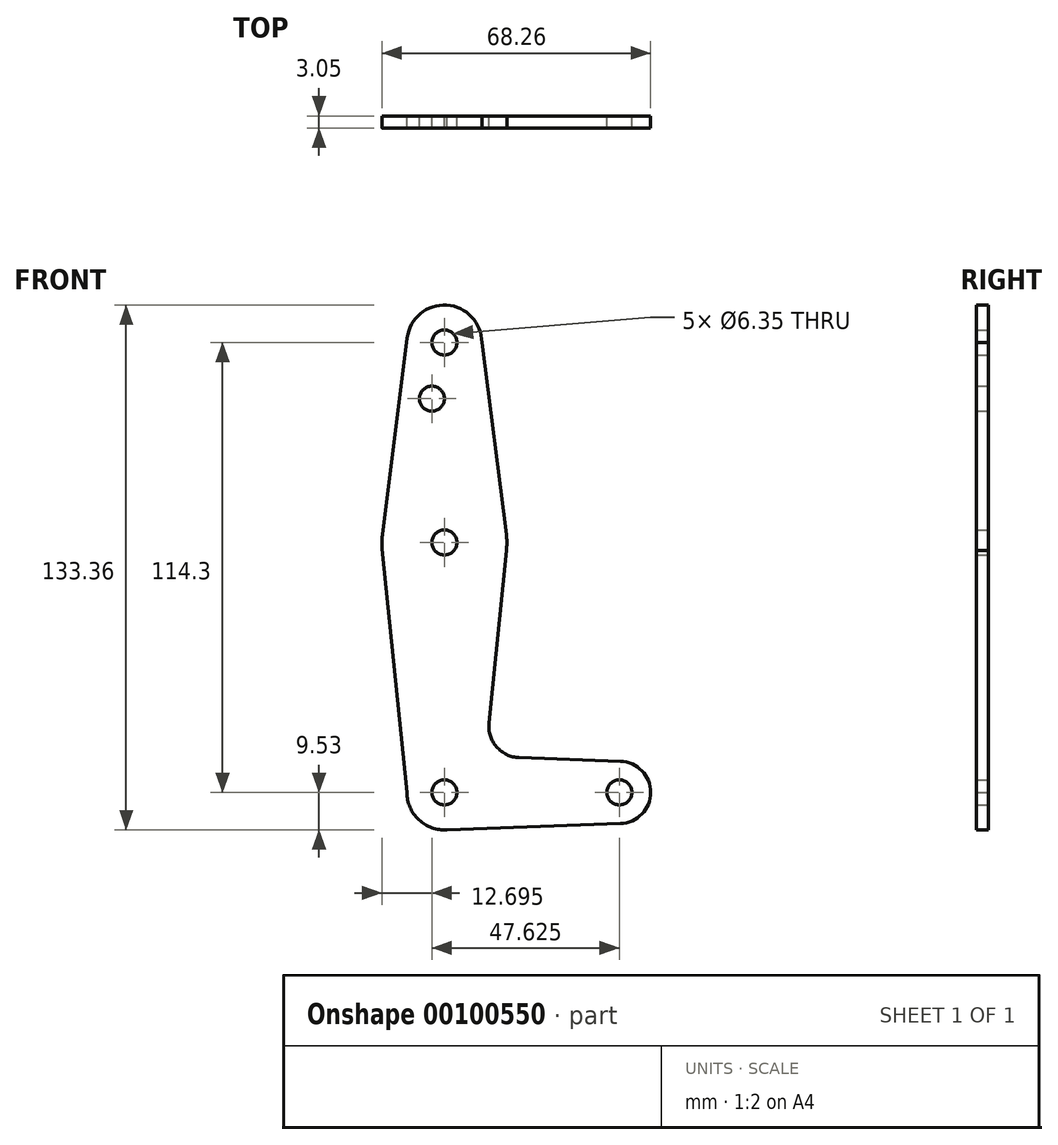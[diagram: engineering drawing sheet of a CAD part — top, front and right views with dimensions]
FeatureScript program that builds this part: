
annotation { "Feature Type Name" : "Feature", "Feature Type Description" : "" }
export const myFeature = defineFeature(function(context is Context, id is Id, definition is map)
    precondition{}
    {
        {
            var Q0;
            Q0=qCreatedBy(makeId("Front.planeOp"),FACE);
            var sketch = newSketch(context, id + "F0", { "sketchPlane" : qUnion([Q0])});
            skLineSegment(sketch, "E0", {"start": v(0, 114.3) * mm, "end": v(0, 0) * mm, "construction": true});
            skLineSegment(sketch, "E1", {"start": v(0, 0) * mm, "end": v(44.45, 0) * mm, "construction": true});
            skCircle(sketch, "E2", {"center": v(0, 114.3) * mm, "radius": 9.53 * mm});
            skCircle(sketch, "E3", {"center": v(0, 63.5) * mm, "radius": 15.88 * mm});
            skCircle(sketch, "E4", {"center": v(0, 0) * mm, "radius": 9.53 * mm});
            skCircle(sketch, "E5", {"center": v(44.45, 0) * mm, "radius": 7.94 * mm});
            skLineSegment(sketch, "E6", {"start": v(9.52, 114.3) * mm, "end": v(15.75, 65.5) * mm});
            skLineSegment(sketch, "E7", {"start": v(-9.45, 115.5) * mm, "end": v(-15.75, 65.48) * mm});
            skLineSegment(sketch, "E8", {"start": v(15.75, 61.5) * mm, "end": v(11.34, 17.59) * mm});
            skLineSegment(sketch, "E9", {"start": v(-9.52, 0) * mm, "end": v(-15.8, 61.9) * mm});
            skLineSegment(sketch, "E10", {"start": v(0, -9.53) * mm, "end": v(44.73, -7.93) * mm});
            skLineSegment(sketch, "E11", {"start": v(18.97, 8.85) * mm, "end": v(44.73, 7.93) * mm});
            skCircle(sketch, "E12", {"center": v(0, 114.3) * mm, "radius": 3.18 * mm});
            skCircle(sketch, "E13", {"center": v(-3.17, 100.03) * mm, "radius": 3.18 * mm});
            skCircle(sketch, "E14", {"center": v(0, 63.5) * mm, "radius": 3.18 * mm});
            skCircle(sketch, "E15", {"center": v(0, 0) * mm, "radius": 3.18 * mm});
            skCircle(sketch, "E16", {"center": v(44.45, 0) * mm, "radius": 3.18 * mm});
            skArc(sketch, "E17.filletArc", {"start": v(11.34, 17.59) * mm, "mid": v(13.26, 11.57) * mm, "end": v(18.97, 8.85) * mm});
            skSolve(sketch);
        }
        {
            var Q0;
            Q0 = qSketchRegion(id + "F0", true);
            extrude(context, id + "F1", {"entities" : qUnion([Q0]), "depth" : 3.05 * mm});
        }
    });
